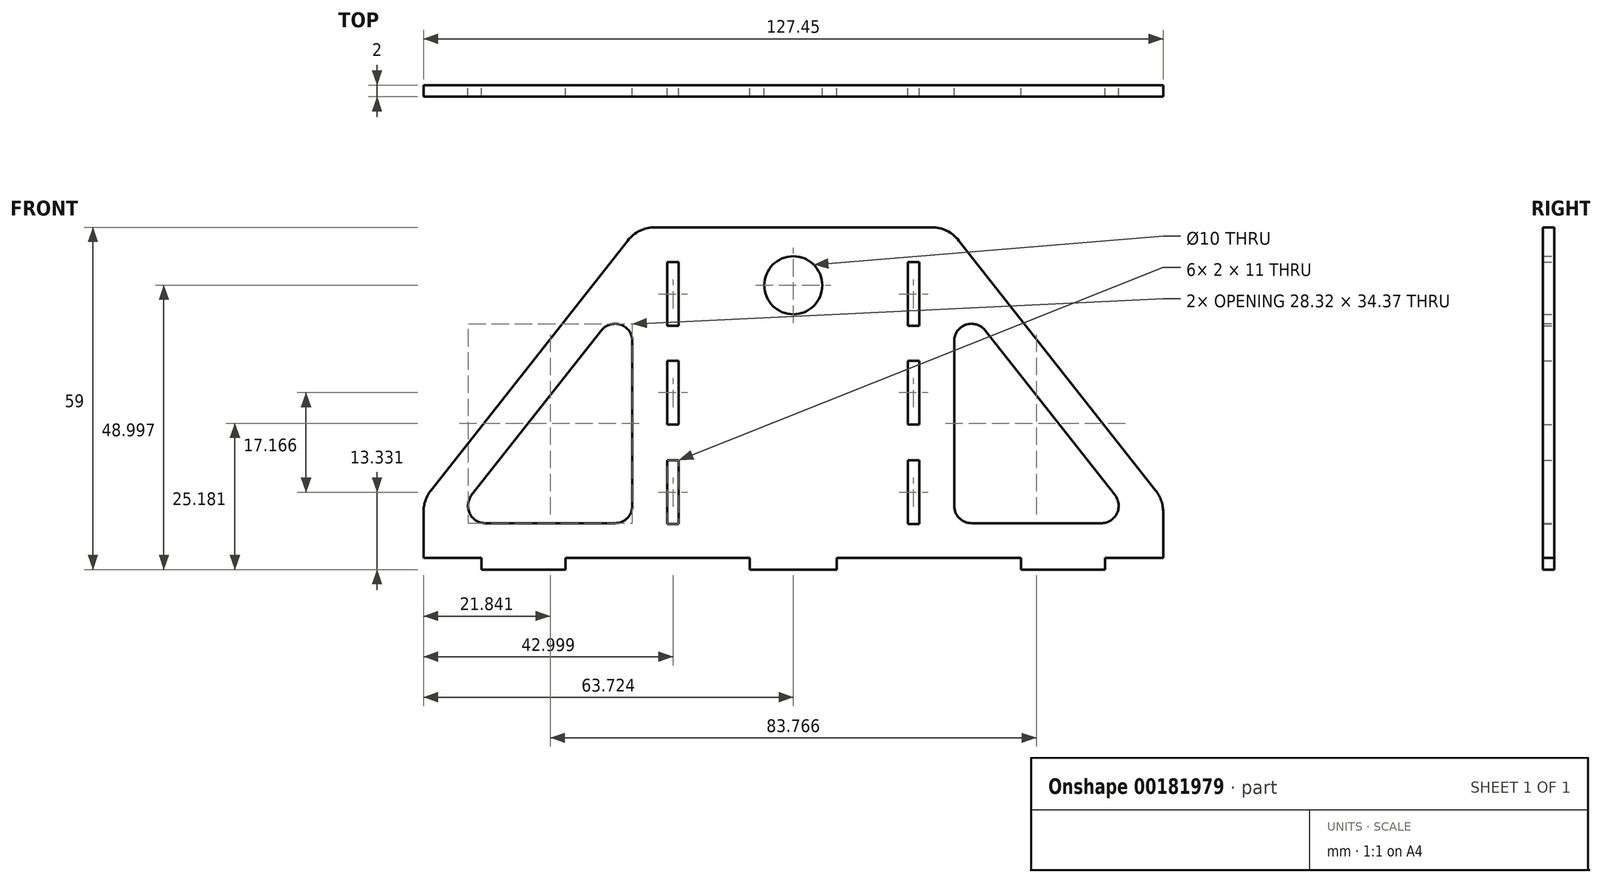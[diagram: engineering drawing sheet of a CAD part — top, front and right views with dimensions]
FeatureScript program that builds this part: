
annotation { "Feature Type Name" : "Feature", "Feature Type Description" : "" }
export const myFeature = defineFeature(function(context is Context, id is Id, definition is map)
    precondition{}
    {
        {
            var Q0;
            Q0=qCreatedBy(makeId("Front.planeOp"),FACE);
            var sketch = newSketch(context, id + "F0", { "sketchPlane" : qUnion([Q0])});
            skLineSegment(sketch, "E0.bottom", {"start": v(-19.58, 35.32) * mm, "end": v(0.14, 35.32) * mm});
            skLineSegment(sketch, "E0.left", {"start": v(-19.58, 29.32) * mm, "end": v(-19.58, 18.32) * mm});
            skLineSegment(sketch, "E1.bottom", {"start": v(-19.58, 35.32) * mm, "end": v(-21.58, 35.32) * mm});
            skLineSegment(sketch, "E1.top", {"start": v(-19.58, -21.69) * mm, "end": v(-21.58, -21.69) * mm});
            skLineSegment(sketch, "E2.bottom", {"start": v(-21.58, 35.32) * mm, "end": v(-23.67, 35.32) * mm});
            skLineSegment(sketch, "E2.top", {"start": v(-21.58, -21.68) * mm, "end": v(-39.08, -21.68) * mm});
            skLineSegment(sketch, "E2.left", {"start": v(-21.58, 29.32) * mm, "end": v(-21.58, 18.32) * mm});
            skLineSegment(sketch, "E2.right", {"start": v(-63.58, -13.76) * mm, "end": v(-63.58, -21.68) * mm});
            skLineSegment(sketch, "E3.top", {"start": v(-7.33, -23.68) * mm, "end": v(0.14, -23.68) * mm});
            skLineSegment(sketch, "E3.left", {"start": v(-7.33, -21.85) * mm, "end": v(-7.33, -23.68) * mm});
            skLineSegment(sketch, "E4.top", {"start": v(-39.08, -23.68) * mm, "end": v(-53.58, -23.68) * mm});
            skLineSegment(sketch, "E4.left", {"start": v(-39.08, -21.68) * mm, "end": v(-39.08, -23.68) * mm});
            skLineSegment(sketch, "E4.right", {"start": v(-53.58, -21.68) * mm, "end": v(-53.58, -23.68) * mm});
            skLineSegment(sketch, "E5", {"start": v(-62.3, -10.05) * mm, "end": v(-28.38, 33.03) * mm});
            skCircle(sketch, "E6", {"center": v(0.14, 25.32) * mm, "radius": 5 * mm});
            skPoint(sketch, "E7.visualSharp", {"position": v(-26.58, 35.32) * mm});
            skArc(sketch, "E7.filletArc", {"start": v(-23.67, 35.32) * mm, "mid": v(-26.29, 34.71) * mm, "end": v(-28.38, 33.03) * mm});
            skPoint(sketch, "E8.visualSharp", {"position": v(-63.58, -11.68) * mm});
            skArc(sketch, "E8.filletArc", {"start": v(-62.3, -10.05) * mm, "mid": v(-63.25, -11.8) * mm, "end": v(-63.58, -13.76) * mm});
            skLineSegment(sketch, "E9", {"start": v(-21.58, 29.32) * mm, "end": v(-19.58, 29.32) * mm});
            skLineSegment(sketch, "E10", {"start": v(-21.58, 18.32) * mm, "end": v(-19.58, 18.32) * mm});
            skLineSegment(sketch, "E11", {"start": v(-21.58, 12.32) * mm, "end": v(-19.58, 12.32) * mm});
            skLineSegment(sketch, "E12", {"start": v(-21.58, -15.85) * mm, "end": v(-19.58, -15.85) * mm});
            skLineSegment(sketch, "E13.trimOffspring", {"start": v(-53.58, -21.68) * mm, "end": v(-63.58, -21.68) * mm});
            skLineSegment(sketch, "E14.trimOffspring", {"start": v(-19.58, 12.32) * mm, "end": v(-19.58, 1.32) * mm});
            skLineSegment(sketch, "E15.trimOffspring", {"start": v(-21.58, 12.32) * mm, "end": v(-21.58, 1.32) * mm});
            skLineSegment(sketch, "E16", {"start": v(-21.58, -4.85) * mm, "end": v(-19.58, -4.85) * mm});
            skLineSegment(sketch, "E17", {"start": v(-21.58, 1.32) * mm, "end": v(-19.58, 1.32) * mm});
            skLineSegment(sketch, "E18", {"start": v(-52.91, -15.68) * mm, "end": v(-30.58, -15.68) * mm});
            skLineSegment(sketch, "E19", {"start": v(-27.58, -12.68) * mm, "end": v(-27.58, 15.69) * mm});
            skLineSegment(sketch, "E20", {"start": v(-32.94, 17.54) * mm, "end": v(-55.27, -10.83) * mm});
            skPoint(sketch, "E21.visualSharp", {"position": v(-27.58, 24.35) * mm});
            skArc(sketch, "E21.filletArc", {"start": v(-27.58, 15.69) * mm, "mid": v(-29.6, 18.52) * mm, "end": v(-32.94, 17.54) * mm});
            skPoint(sketch, "E22.visualSharp", {"position": v(-27.58, -15.68) * mm});
            skArc(sketch, "E22.filletArc", {"start": v(-30.58, -15.68) * mm, "mid": v(-28.46, -14.8) * mm, "end": v(-27.58, -12.68) * mm});
            skArc(sketch, "E23.filletArc", {"start": v(-55.27, -10.83) * mm, "mid": v(-55.61, -14) * mm, "end": v(-52.91, -15.68) * mm});
            skLineSegment(sketch, "E24", {"start": v(0.14, 53.67) * mm, "end": v(0.14, -31.15) * mm});
            skLineSegment(sketch, "E25", {"start": v(0.14, -31.15) * mm, "end": v(0.45, -31.15) * mm});
            skPoint(sketch, "E3.right.end.orphan", {"position": v(7.17, -23.68) * mm});
            skLineSegment(sketch, "E26.trimOffspring", {"start": v(-21.58, -4.85) * mm, "end": v(-21.58, -15.85) * mm});
            skLineSegment(sketch, "E27.trimOffspring", {"start": v(-19.58, -4.85) * mm, "end": v(-19.58, -15.85) * mm});
            skLineSegment(sketch, "E28.MirrorCS", {"start": v(7.62, -23.68) * mm, "end": v(0.14, -23.68) * mm});
            skLineSegment(sketch, "E29.MirrorCS", {"start": v(19.87, 35.32) * mm, "end": v(0.14, 35.32) * mm});
            skLineSegment(sketch, "E30.MirrorCS", {"start": v(21.87, 29.32) * mm, "end": v(19.87, 29.32) * mm});
            skLineSegment(sketch, "E31.MirrorCS", {"start": v(21.87, -15.85) * mm, "end": v(19.87, -15.85) * mm});
            skLineSegment(sketch, "E32.MirrorCS", {"start": v(21.87, 12.32) * mm, "end": v(19.87, 12.32) * mm});
            skLineSegment(sketch, "E33.MirrorCS", {"start": v(7.62, -21.85) * mm, "end": v(7.62, -23.68) * mm});
            skLineSegment(sketch, "E34.MirrorCS", {"start": v(21.87, 1.32) * mm, "end": v(19.87, 1.32) * mm});
            skLineSegment(sketch, "E35.MirrorCS", {"start": v(21.87, 18.32) * mm, "end": v(19.87, 18.32) * mm});
            skLineSegment(sketch, "E36.MirrorCS", {"start": v(53.87, -21.68) * mm, "end": v(53.87, -23.68) * mm});
            skLineSegment(sketch, "E37.MirrorCS", {"start": v(21.87, -4.85) * mm, "end": v(19.87, -4.85) * mm});
            skLineSegment(sketch, "E38.MirrorCS", {"start": v(39.37, -21.68) * mm, "end": v(39.37, -23.68) * mm});
            skLineSegment(sketch, "E39.MirrorCS", {"start": v(19.87, 35.32) * mm, "end": v(21.87, 35.32) * mm});
            skLineSegment(sketch, "E40.MirrorCS", {"start": v(21.87, 35.32) * mm, "end": v(23.96, 35.32) * mm});
            skArc(sketch, "E41.MirrorCS", {"start": v(23.96, 35.32) * mm, "mid": v(26.58, 34.71) * mm, "end": v(28.67, 33.03) * mm});
            skArc(sketch, "E42.MirrorCS", {"start": v(30.87, -15.68) * mm, "mid": v(28.75, -14.8) * mm, "end": v(27.87, -12.68) * mm});
            skLineSegment(sketch, "E43.MirrorCS", {"start": v(19.87, 29.32) * mm, "end": v(19.87, 18.32) * mm});
            skLineSegment(sketch, "E44.MirrorCS", {"start": v(21.87, -4.85) * mm, "end": v(21.87, -15.85) * mm});
            skLineSegment(sketch, "E45.MirrorCS", {"start": v(19.87, -4.85) * mm, "end": v(19.87, -15.85) * mm});
            skArc(sketch, "E46.MirrorCS", {"start": v(62.58, -10.05) * mm, "mid": v(63.54, -11.8) * mm, "end": v(63.87, -13.76) * mm});
            skLineSegment(sketch, "E47.MirrorCS", {"start": v(21.87, 12.32) * mm, "end": v(21.87, 1.32) * mm});
            skPoint(sketch, "E48.MirrorP", {"position": v(27.87, 24.35) * mm});
            skLineSegment(sketch, "E49.MirrorCS", {"start": v(63.87, -13.76) * mm, "end": v(63.87, -21.68) * mm});
            skLineSegment(sketch, "E50.MirrorCS", {"start": v(21.87, -21.68) * mm, "end": v(39.37, -21.68) * mm});
            skLineSegment(sketch, "E51.MirrorCS", {"start": v(19.87, 12.32) * mm, "end": v(19.87, 1.32) * mm});
            skLineSegment(sketch, "E52.MirrorCS", {"start": v(62.58, -10.05) * mm, "end": v(28.67, 33.03) * mm});
            skLineSegment(sketch, "E53.MirrorCS", {"start": v(21.87, 29.32) * mm, "end": v(21.87, 18.32) * mm});
            skPoint(sketch, "E54.MirrorP", {"position": v(27.87, -15.68) * mm});
            skArc(sketch, "E55.MirrorCS", {"start": v(55.56, -10.83) * mm, "mid": v(55.9, -14) * mm, "end": v(53.2, -15.68) * mm});
            skArc(sketch, "E56.MirrorCS", {"start": v(27.87, 15.69) * mm, "mid": v(29.89, 18.52) * mm, "end": v(33.23, 17.54) * mm});
            skLineSegment(sketch, "E57.MirrorCS", {"start": v(33.23, 17.54) * mm, "end": v(55.56, -10.83) * mm});
            skLineSegment(sketch, "E58.MirrorCS", {"start": v(53.87, -21.68) * mm, "end": v(63.87, -21.68) * mm});
            skLineSegment(sketch, "E59.MirrorCS", {"start": v(53.2, -15.68) * mm, "end": v(30.87, -15.68) * mm});
            skLineSegment(sketch, "E60.MirrorCS", {"start": v(39.37, -23.68) * mm, "end": v(53.87, -23.68) * mm});
            skLineSegment(sketch, "E61.MirrorCS", {"start": v(27.87, -12.68) * mm, "end": v(27.87, 15.69) * mm});
            skPoint(sketch, "E62.MirrorP", {"position": v(63.87, -11.68) * mm});
            skPoint(sketch, "E63.MirrorP", {"position": v(26.87, 35.32) * mm});
            skLineSegment(sketch, "E64", {"start": v(-63.58, -21.68) * mm, "end": v(-53.58, -21.68) * mm});
            skLineSegment(sketch, "E65", {"start": v(-7.33, -21.85) * mm, "end": v(-7.33, -21.68) * mm});
            skLineSegment(sketch, "E66", {"start": v(7.62, -21.85) * mm, "end": v(7.62, -21.68) * mm});
            skLineSegment(sketch, "E67.trimOffspring", {"start": v(7.62, -21.68) * mm, "end": v(39.37, -21.68) * mm});
            skLineSegment(sketch, "E68.trimOffspring", {"start": v(-39.08, -21.68) * mm, "end": v(-7.33, -21.68) * mm});
            skSolve(sketch);
        }
        {
            var Q0;
            {var subQ2=sQuery(id+"F0.wireOp",EDGE,"E0.bottom");Q0=makeQuery(id+"F0.imprint","IMPRINT",FACE,{"disambiguationData":[TD([[makeQuery(id+"F0.imprint","IMPRINT",EDGE,{"derivedFrom":subQ2}),-1.0]])]});}
            var Q1;
            {var subQ6=sQuery(id+"F0.wireOp",EDGE,"E28.MirrorCS");Q1=makeQuery(id+"F0.imprint","IMPRINT",FACE,{"disambiguationData":[TD([[makeQuery(id+"F0.imprint","IMPRINT",EDGE,{"derivedFrom":subQ6}),-1.0]])]});}
            extrude(context, id + "F1", {"entities" : qUnion([Q0, Q1]), "depth" : 2 * mm});
        }
    });
